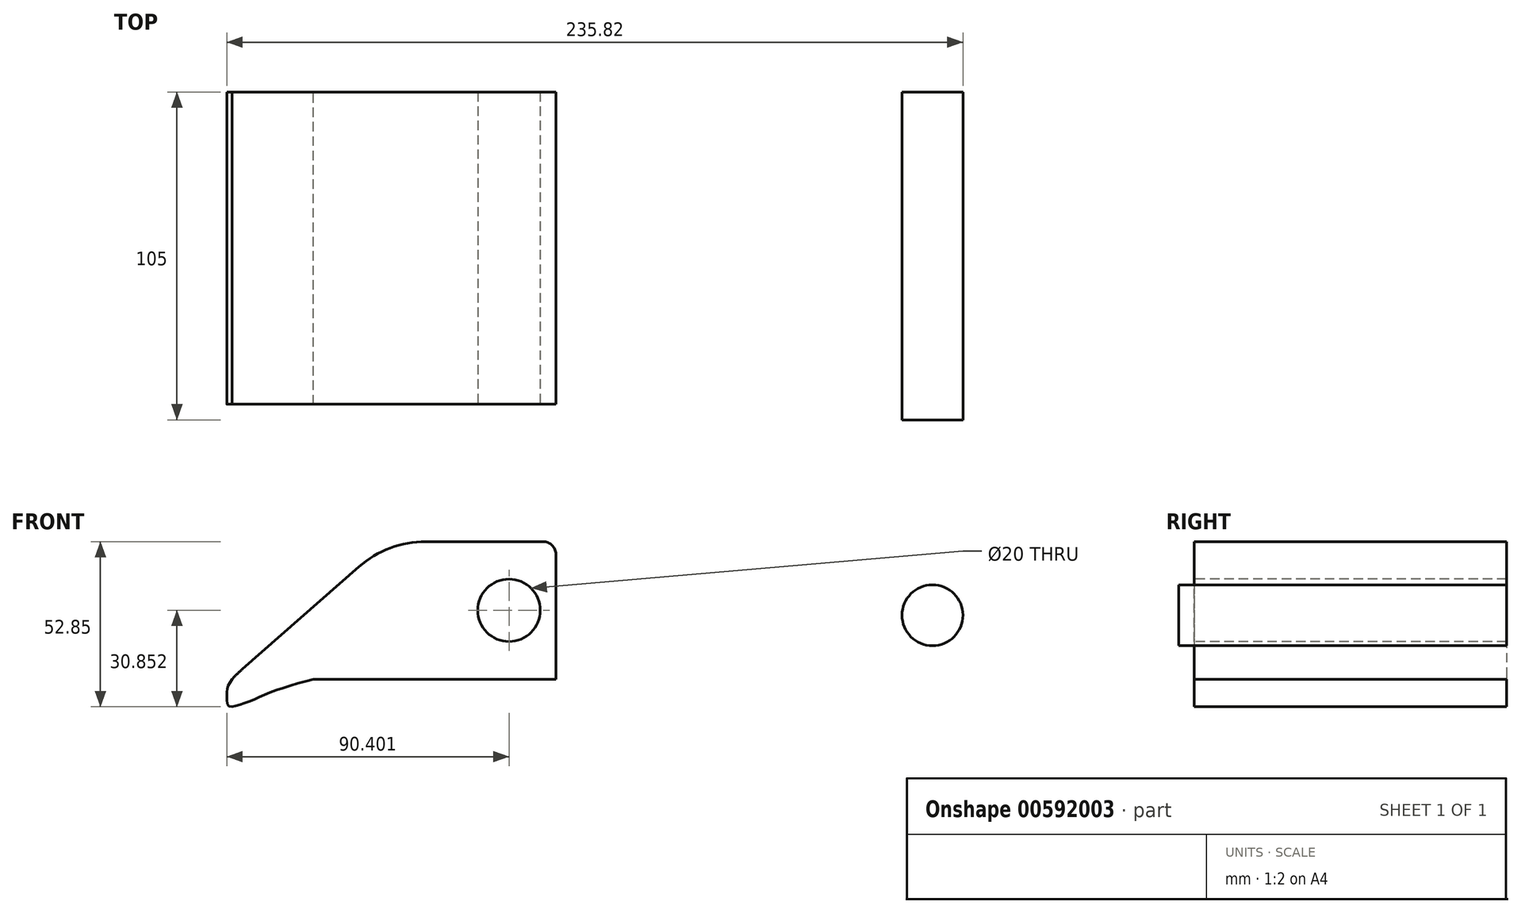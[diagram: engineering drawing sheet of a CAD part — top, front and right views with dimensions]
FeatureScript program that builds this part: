
annotation { "Feature Type Name" : "Feature", "Feature Type Description" : "" }
export const myFeature = defineFeature(function(context is Context, id is Id, definition is map)
    precondition{}
    {
        {
            var Q0;
            Q0=qCreatedBy(makeId("Front.planeOp"),FACE);
            var sketch = newSketch(context, id + "F0", { "sketchPlane" : qUnion([Q0])});
            skLineSegment(sketch, "E0", {"start": v(-1324.94, -512.42) * mm, "end": v(-1287.36, -512.42) * mm});
            skLineSegment(sketch, "E1", {"start": v(-1283.3, -516.47) * mm, "end": v(-1283.3, -556.47) * mm});
            skLineSegment(sketch, "E2", {"start": v(-1346.38, -520.5) * mm, "end": v(-1383.68, -553.25) * mm});
            skLineSegment(sketch, "E3", {"start": v(-1283.3, -556.47) * mm, "end": v(-1387.08, -556.47) * mm});
            skLineSegment(sketch, "E4", {"start": v(-1386.24, -555.64) * mm, "end": v(-1387.08, -556.47) * mm});
            skPoint(sketch, "E5.visualSharp", {"position": v(-1337.18, -512.42) * mm});
            skArc(sketch, "E5.filletArc", {"start": v(-1324.94, -512.42) * mm, "mid": v(-1336.4, -514.5) * mm, "end": v(-1346.38, -520.5) * mm});
            skPoint(sketch, "E6.visualSharp", {"position": v(-1385, -554.4) * mm});
            skArc(sketch, "E6.filletArc", {"start": v(-1383.68, -553.25) * mm, "mid": v(-1384.98, -554.43) * mm, "end": v(-1386.24, -555.64) * mm});
            skPoint(sketch, "E7.visualSharp", {"position": v(-1283.3, -512.42) * mm});
            skArc(sketch, "E7.filletArc", {"start": v(-1283.3, -516.47) * mm, "mid": v(-1284.5, -513.6) * mm, "end": v(-1287.36, -512.42) * mm});
            skFitSpline(sketch, "E8", {"points": [v(-1387.08, -556.47) * mm, v(-1388.5, -559.2) * mm, v(-1388.71, -561.73) * mm, v(-1388.22, -564.94) * mm, v(-1385.97, -565.07) * mm, v(-1380.96, -563.4) * mm, v(-1373.75, -560.33) * mm, v(-1360.94, -556.47) * mm], "startDerivative": vector(-15.2, -24.48) * mm, "endDerivative": vector(57.9, 15.7) * mm});
            skSolve(sketch);
        }
        {
            var Q0;
            Q0 = qSketchRegion(id + "F0", true);
            extrude(context, id + "F1", {"entities" : qUnion([Q0]), "depth" : 100 * mm, "offsetDistance" : 25 * mm});
        }
        {
            var Q0;
            Q0=makeQuery(id+"F1.opExtrude","CAP_FACE",FACE,{"disambiguationData":[OSD([sQuery(id+"F0.wireOp",EDGE,"E0"),sQuery(id+"F0.wireOp",EDGE,"E1"),sQuery(id+"F0.wireOp",EDGE,"E2"),sQuery(id+"F0.wireOp",EDGE,"E3"),sQuery(id+"F0.wireOp",EDGE,"E4"),sQuery(id+"F0.wireOp",EDGE,"E5.filletArc"),sQuery(id+"F0.wireOp",EDGE,"E6.filletArc"),sQuery(id+"F0.wireOp",EDGE,"E7.filletArc")])],"isStart":false});
            var sketch = newSketch(context, id + "F2", { "sketchPlane" : qUnion([Q0])});
            skCircle(sketch, "E9", {"center": v(-1298.3, -534.42) * mm, "radius": 10 * mm});
            skSolve(sketch);
        }
        {
            var Q0;
            Q0=makeQuery(id+"F2.imprint","IMPRINT",FACE,{"disambiguationData":[TD([[makeQuery(id+"F2.imprint","IMPRINT",EDGE,{"derivedFrom":sQuery(id+"F2.wireOp",EDGE,"E9")}),1.0]])]});
            extrude(context, id + "F3", {"entities" : qUnion([Q0]), "operationType" : NewBodyOperationType.REMOVE, "oppositeDirection" : true, "depth" : 200 * mm, "offsetDistance" : 25 * mm});
        }
        {
            var Q0;
            Q0=qCreatedBy(makeId("Front.planeOp"),FACE);
            var sketch = newSketch(context, id + "F4", { "sketchPlane" : qUnion([Q0])});
            skCircle(sketch, "E10", {"center": v(-1162.64, -536) * mm, "radius": 9.75 * mm});
            skSolve(sketch);
        }
        {
            var Q0;
            Q0=makeQuery(id+"F4.imprint","IMPRINT",FACE,{"disambiguationData":[TD([[makeQuery(id+"F4.imprint","IMPRINT",EDGE,{"derivedFrom":sQuery(id+"F4.wireOp",EDGE,"E10")}),1.0]])]});
            extrude(context, id + "F5", {"entities" : qUnion([Q0]), "depth" : 105 * mm, "offsetDistance" : 25 * mm});
        }
    });
